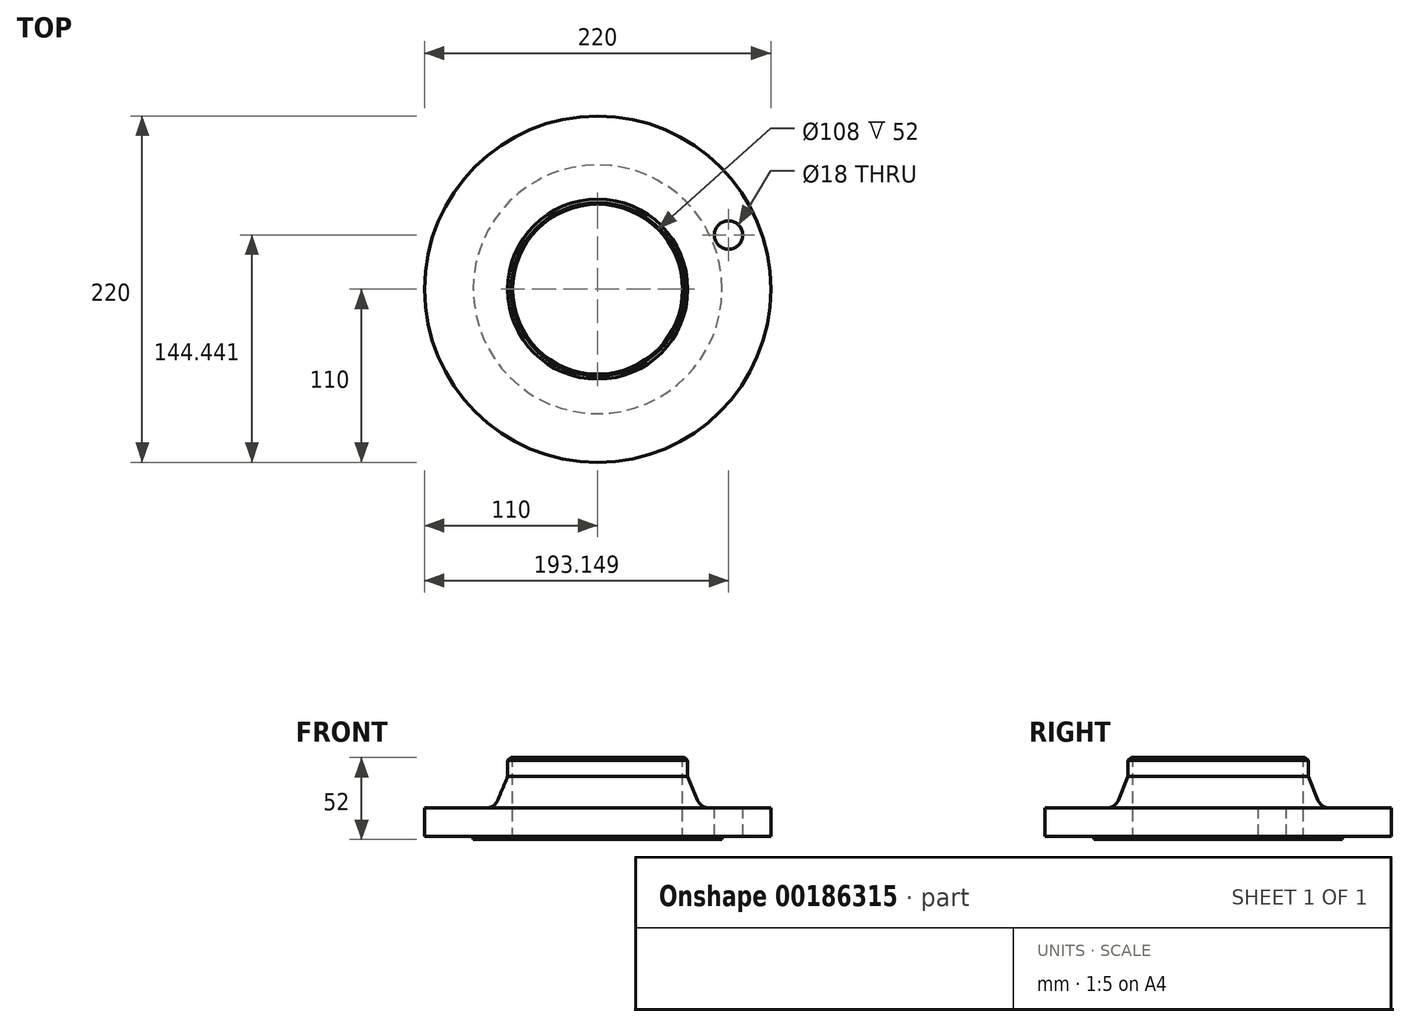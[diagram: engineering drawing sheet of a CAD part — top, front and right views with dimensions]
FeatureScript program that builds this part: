
annotation { "Feature Type Name" : "Feature", "Feature Type Description" : "" }
export const myFeature = defineFeature(function(context is Context, id is Id, definition is map)
    precondition{}
    {
        {
            var Q0;
            Q0=qCreatedBy(makeId("Front.planeOp"),FACE);
            var sketch = newSketch(context, id + "F0", { "sketchPlane" : qUnion([Q0])});
            skLineSegment(sketch, "E0", {"start": v(0, 52) * mm, "end": v(0, 0) * mm});
            skLineSegment(sketch, "E1", {"start": v(54, 0) * mm, "end": v(79, 0) * mm});
            skLineSegment(sketch, "E2", {"start": v(79, 0) * mm, "end": v(79, 2) * mm});
            skLineSegment(sketch, "E3", {"start": v(79, 2) * mm, "end": v(110, 2) * mm});
            skLineSegment(sketch, "E4", {"start": v(110, 2) * mm, "end": v(110, 20) * mm});
            skLineSegment(sketch, "E5", {"start": v(110, 20) * mm, "end": v(65.5, 20) * mm});
            skLineSegment(sketch, "E6", {"start": v(65.5, 20) * mm, "end": v(57.15, 40) * mm});
            skLineSegment(sketch, "E7", {"start": v(57.15, 40) * mm, "end": v(57.15, 52) * mm});
            skLineSegment(sketch, "E8", {"start": v(57.15, 52) * mm, "end": v(54, 52) * mm});
            skLineSegment(sketch, "E9", {"start": v(54, 52) * mm, "end": v(54, 0) * mm});
            skSolve(sketch);
        }
        {
            var Q0;
            Q0=makeQuery(id+"F0.imprint","IMPRINT",FACE,{"disambiguationData":[TD([[makeQuery(id+"F0.imprint","IMPRINT",EDGE,{"derivedFrom":sQuery(id+"F0.wireOp",EDGE,"E1")}),1.0]])]});
            var Q1;
            Q1=sQuery(id+"F0.wireOp",EDGE,"E0");
            revolve(context, id + "F1", {"entities" : qUnion([Q0]), "axis" : qUnion([Q1]), "revolveType" : RevolveType.FULL});
        }
        {
            var Q0;
            Q0=makeQuery(id+"F1.opRevolve","SWEPT_FACE",FACE,{"disambiguationData":[OSD([sQuery(id+"F0.wireOp",EDGE,"E5")])]});
            var sketch = newSketch(context, id + "F2", { "sketchPlane" : qUnion([Q0])});
            skCircle(sketch, "E10", {"center": v(83.15, 34.44) * mm, "radius": 9 * mm});
            skLineSegment(sketch, "E11", {"start": v(83.15, 34.44) * mm, "end": v(0, 0) * mm});
            skSolve(sketch);
        }
        {
            var Q0;
            Q0=makeQuery(id+"F2.imprint","IMPRINT",FACE,{"disambiguationData":[TD([[makeQuery(id+"F2.imprint","IMPRINT",EDGE,{"derivedFrom":sQuery(id+"F2.wireOp",EDGE,"E10")}),1.0]])]});
            extrude(context, id + "F3", {"entities" : qUnion([Q0]), "operationType" : NewBodyOperationType.REMOVE, "endBound" : BoundingType.THROUGH_ALL, "oppositeDirection" : true, "depth" : 25 * mm});
        }
        {
            var Q0;
            Q0=qCreatedBy(makeId("Front.planeOp"),FACE);
            var sketch = newSketch(context, id + "F4", { "sketchPlane" : qUnion([Q0])});
            skLineSegment(sketch, "E12", {"start": v(55, 52) * mm, "end": v(55, 52) * mm});
            skLineSegment(sketch, "E13", {"start": v(55, 52) * mm, "end": v(57.15, 50.35) * mm});
            skLineSegment(sketch, "E14", {"start": v(57.15, 50.35) * mm, "end": v(57.15, 52) * mm});
            skLineSegment(sketch, "E15", {"start": v(57.15, 52) * mm, "end": v(55, 52) * mm});
            skSolve(sketch);
        }
        {
            var Q0;
            Q0 = qSketchRegion(id + "F4", true);
            var Q1;
            Q1=sQuery(id+"F0.wireOp",EDGE,"E0");
            revolve(context, id + "F5", {"operationType" : NewBodyOperationType.REMOVE, "entities" : qUnion([Q0]), "axis" : qUnion([Q1]), "revolveType" : RevolveType.FULL, "oppositeDirection" : true});
        }
        {
            var Q0;
            Q0=makeQuery(id+"F1.opRevolve","SWEPT_EDGE",EDGE,{"disambiguationData":[OSD([sQuery(id+"F0.wireOp",EDGE,"E5"),sQuery(id+"F0.wireOp",EDGE,"E6")])]});
            fillet(context, id + "F6", {"entities" : qUnion([Q0]), "radius" : 8 * mm, "tangentPropagation" : true, "allowEdgeOverflow" : false});
        }
    });
